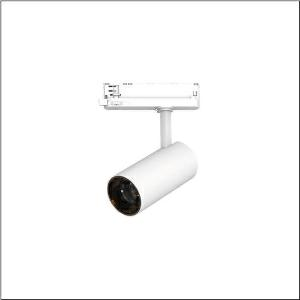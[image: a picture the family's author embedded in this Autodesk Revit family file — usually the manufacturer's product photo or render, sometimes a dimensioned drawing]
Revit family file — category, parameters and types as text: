
# Revit family: spot_31_slim_51sf137fa2b
name_source: partatom
category: Lighting Fixtures
units: mm (PartAtom-declared; Revit-internal decimal feet)

## family parameters
Cut with Voids When Loaded = No
Host = Face
Light Source = No
Part Type = Normal
Room Calculation Point = No
Round Connector Dimension = Use Diameter
Shared = No

## types (1)
- Spot 31 Slim (1 x LED, 2150 lm, 17.6 W, 2700K)
    Apparent Load = 18 VA
    CIE Flux Codes = 97 100 100 100 100
    Color Rendering = 90
    Color Temperature = 2700K
    Default Elevation = 1800 mm
    Description = Spot 31 Slim, directional spotlight, light control with reflector, of aluminium, LED rated luminous flux: 2.150lm, light colour: 927, control gear: ECG, with 3-phase adapter, mains connection: 220..240V, AC, 50/60Hz, housing, of aluminium, traffic white (RAL 9016), diameter: 70mm, adapter, of plastic, protection rating (complete): IP20, insulation class (complete): insulation class I (protective earthing), certification: CE, impact resistance: IK02, packaging unit: 1 piece
    Height = 210 mm
    Lamp = 1 x LED
    Lamp Light Flux = 2150 lm
    Lamp Power = 17.6 W
    Lamp count = 1
    Length = 70 mm
    Luminous efficacy = 122 lm/W
    Manufacturer = Siteco
    ModVariant = No
    Model = 51SF137FA2B
    Mounting Place = Ceiling
    Mounting Type = Pendant
    Number of Poles = 1
    OnlyDefault = Yes
    Power Factor = 1
    Product Name = Spot 31 Slim
    Product group = directional spotlight
    ProductGroupID = 905
    Protection Class = Protection class I
    Protection Degree = IP 20
    RLX_Detail_Level = 1
    RLX_Emergency_Light_Flux = 0 lm
    RLX_Emergency_Type = 0
    RLX_Emergency_Type_DB = No
    RlxData = <blob elided: 14149 chars, md5=fb46c7ff>
    Socket = socket
    Standby Power = 0 W
    System Light Flux = 2150 lm
    System Power = 18 W
    Type Comments = Product without accessories
    Type Image = l_1228468.jpg
    URL = http://relux.com
    VarID = ---
    Voltage = 0 V
    Weight = 0.00 kg
    Width = 0 mm  [stored 0 ft]

note: [stored X ft] marks values corroborated as IEEE doubles in the binary element streams (Revit-internal decimal feet)

## geometry (parser evidence)
native form markers: Sweep x10
no freeform markers — native parametric forms only
